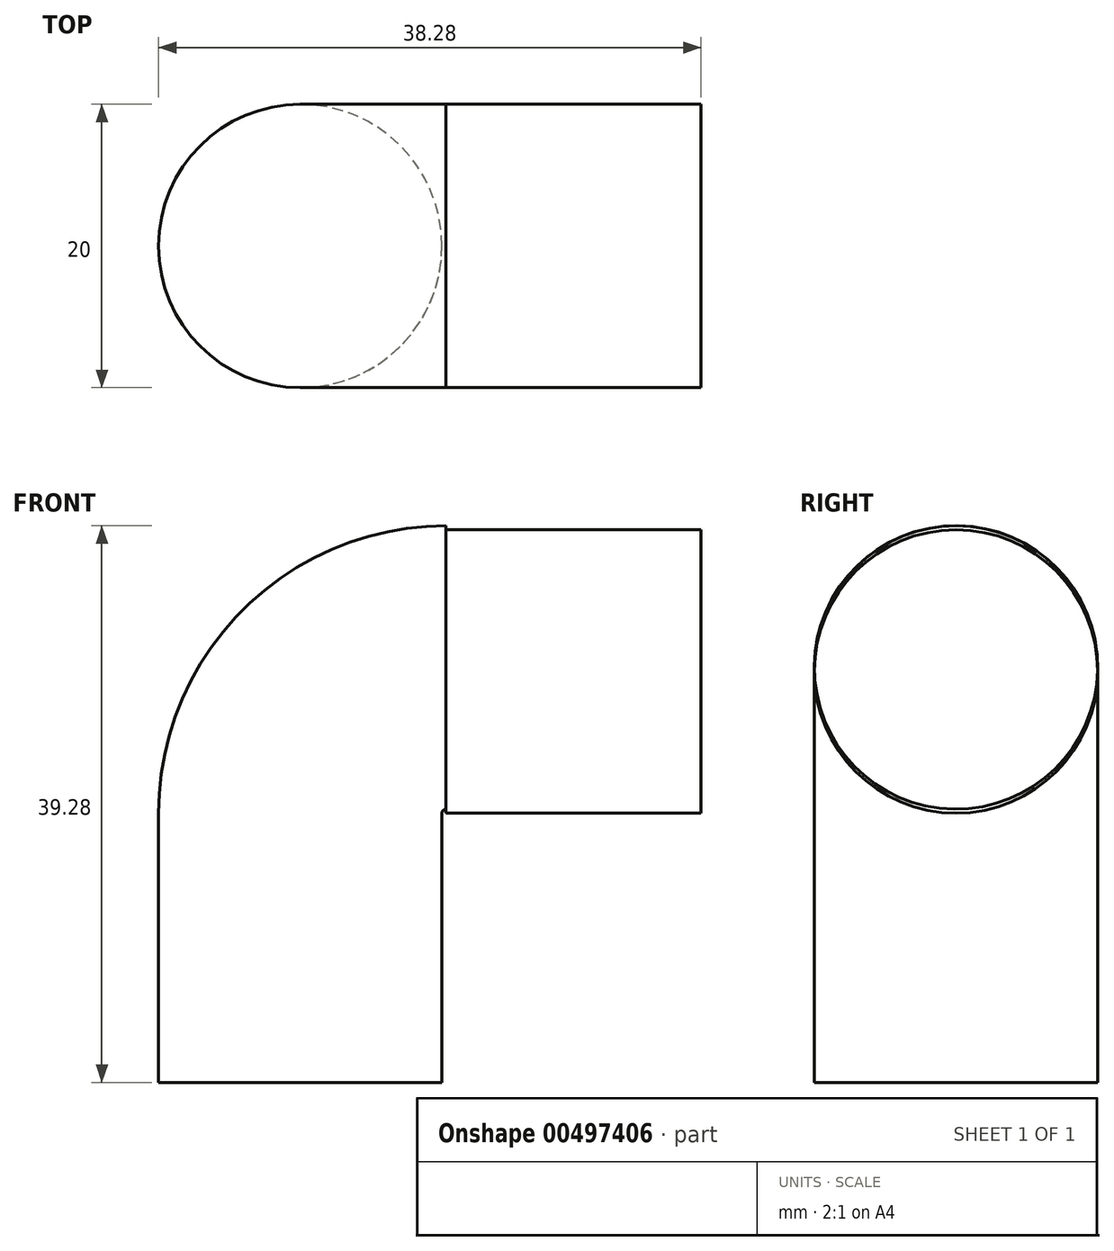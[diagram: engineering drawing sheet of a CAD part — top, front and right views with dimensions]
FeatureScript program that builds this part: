
annotation { "Feature Type Name" : "Feature", "Feature Type Description" : "" }
export const myFeature = defineFeature(function(context is Context, id is Id, definition is map)
    precondition{}
    {
        {
            var Q0;
            Q0=qCreatedBy(makeId("Top.planeOp"),FACE);
            var sketch = newSketch(context, id + "F0", { "sketchPlane" : qUnion([Q0])});
            skCircle(sketch, "E0", {"center": v(-28.28, 10) * mm, "radius": 10 * mm});
            skSolve(sketch);
        }
        {
            var Q0;
            Q0=qCreatedBy(makeId("Right.planeOp"),FACE);
            var sketch = newSketch(context, id + "F1", { "sketchPlane" : qUnion([Q0])});
            skCircle(sketch, "E1", {"center": v(10, 10) * mm, "radius": 10 * mm});
            skSolve(sketch);
        }
        {
            var Q0;
            Q0=makeQuery(id+"F1.imprint","IMPRINT",FACE,{"disambiguationData":[TD([[makeQuery(id+"F1.imprint","IMPRINT",EDGE,{"derivedFrom":sQuery(id+"F1.wireOp",EDGE,"E1")}),1.0]])]});
            extrude(context, id + "F2", {"entities" : qUnion([Q0]), "oppositeDirection" : true, "depth" : 18 * mm});
        }
        {
            var Q0;
            Q0=makeQuery(id+"F0.imprint","IMPRINT",FACE,{"disambiguationData":[TD([[makeQuery(id+"F0.imprint","IMPRINT",EDGE,{"derivedFrom":sQuery(id+"F0.wireOp",EDGE,"E0")}),1.0]])]});
            var Q1;
            Q1=sQuery(id+"F0.wireOp",EDGE,"E0");
            extrude(context, id + "F3", {"entities" : qUnion([Q0]), "surfaceEntities" : qUnion([Q1]), "oppositeDirection" : true, "depth" : 19 * mm});
        }
        {
            var Q0;
            Q0=makeQuery(id+"F2.opExtrude","CAP_FACE",FACE,{"disambiguationData":[OSD([sQuery(id+"F1.wireOp",EDGE,"E1")])],"isStart":false});
            var sketch = newSketch(context, id + "F4", { "sketchPlane" : qUnion([Q0])});
            skLineSegment(sketch, "E2", {"start": v(-54.6, 0) * mm, "end": v(39.82, 0) * mm, "construction": true});
            skSolve(sketch);
        }
        {
            var Q0;
            Q0=makeQuery(id+"F3.opExtrude","CAP_FACE",FACE,{"disambiguationData":[OSD([sQuery(id+"F0.wireOp",EDGE,"E0")])],"isStart":true});
            var Q1;
            Q1=sQuery(id+"F4.wireOp",EDGE,"E2");
            revolve(context, id + "F5", {"operationType" : NewBodyOperationType.ADD, "entities" : qUnion([Q0]), "axis" : qUnion([Q1]), "revolveType" : RevolveType.ONE_DIRECTION, "oppositeDirection" : true, "angle" : 90 * degree});
        }
    });
